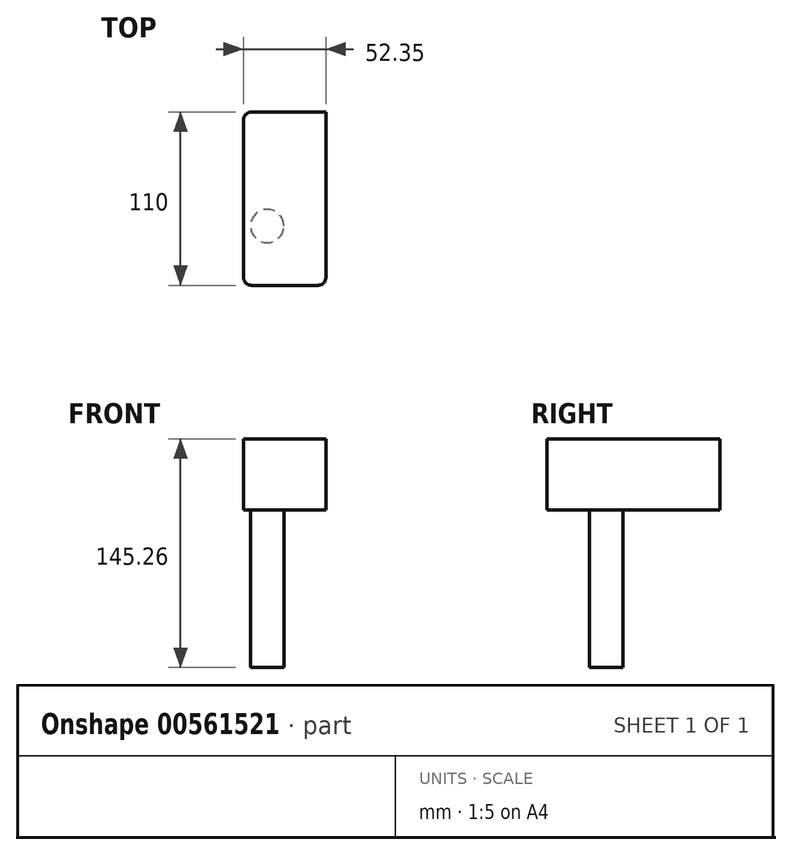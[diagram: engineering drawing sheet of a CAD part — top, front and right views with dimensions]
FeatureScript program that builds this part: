
annotation { "Feature Type Name" : "Feature", "Feature Type Description" : "" }
export const myFeature = defineFeature(function(context is Context, id is Id, definition is map)
    precondition{}
    {
        {
            var Q0;
            Q0=qCreatedBy(makeId("Front.planeOp"),FACE);
            var sketch = newSketch(context, id + "F0", { "sketchPlane" : qUnion([Q0])});
            skLineSegment(sketch, "E0.bottom", {"start": v(0, 0) * mm, "end": v(52.35, 0) * mm});
            skLineSegment(sketch, "E0.top", {"start": v(0, 45.26) * mm, "end": v(52.35, 45.26) * mm});
            skLineSegment(sketch, "E0.left", {"start": v(0, 0) * mm, "end": v(0, 45.26) * mm});
            skLineSegment(sketch, "E0.right", {"start": v(52.35, 0) * mm, "end": v(52.35, 45.26) * mm});
            skSolve(sketch);
        }
        {
            var Q0;
            Q0 = qSketchRegion(id + "F0", true);
            extrude(context, id + "F1", {"entities" : qUnion([Q0]), "depth" : 110 * mm, "offsetDistance" : 25 * mm, "symmetric" : true});
        }
        {
            var Q0;
            Q0=makeQuery(id+"F1.opExtrude","CAP_EDGE",EDGE,{"disambiguationData":[OSD([sQuery(id+"F0.wireOp",EDGE,"E0.right")])],"isStart":false});
            var Q1;
            Q1=makeQuery(id+"F1.opExtrude","CAP_EDGE",EDGE,{"disambiguationData":[OSD([sQuery(id+"F0.wireOp",EDGE,"E0.left")])],"isStart":false});
            var Q2;
            Q2=makeQuery(id+"F1.opExtrude","CAP_EDGE",EDGE,{"disambiguationData":[OSD([sQuery(id+"F0.wireOp",EDGE,"E0.left")])],"isStart":true});
            fillet(context, id + "F2", {"entities" : qUnion([Q0, Q1, Q2]), "radius" : 5 * mm, "tangentPropagation" : true, "allowEdgeOverflow" : false});
        }
        {
            var Q0;
            Q0=makeQuery(id+"F1.opExtrude","SWEPT_FACE",FACE,{"disambiguationData":[OSD([sQuery(id+"F0.wireOp",EDGE,"E0.bottom")])]});
            var sketch = newSketch(context, id + "F3", { "sketchPlane" : qUnion([Q0])});
            skCircle(sketch, "E1", {"center": v(15.05, 17.33) * mm, "radius": 10.59 * mm});
            skSolve(sketch);
        }
        {
            var Q0;
            Q0 = qSketchRegion(id + "F3", true);
            extrude(context, id + "F4", {"entities" : qUnion([Q0]), "operationType" : NewBodyOperationType.ADD, "depth" : 100 * mm, "offsetDistance" : 25 * mm});
        }
    });
